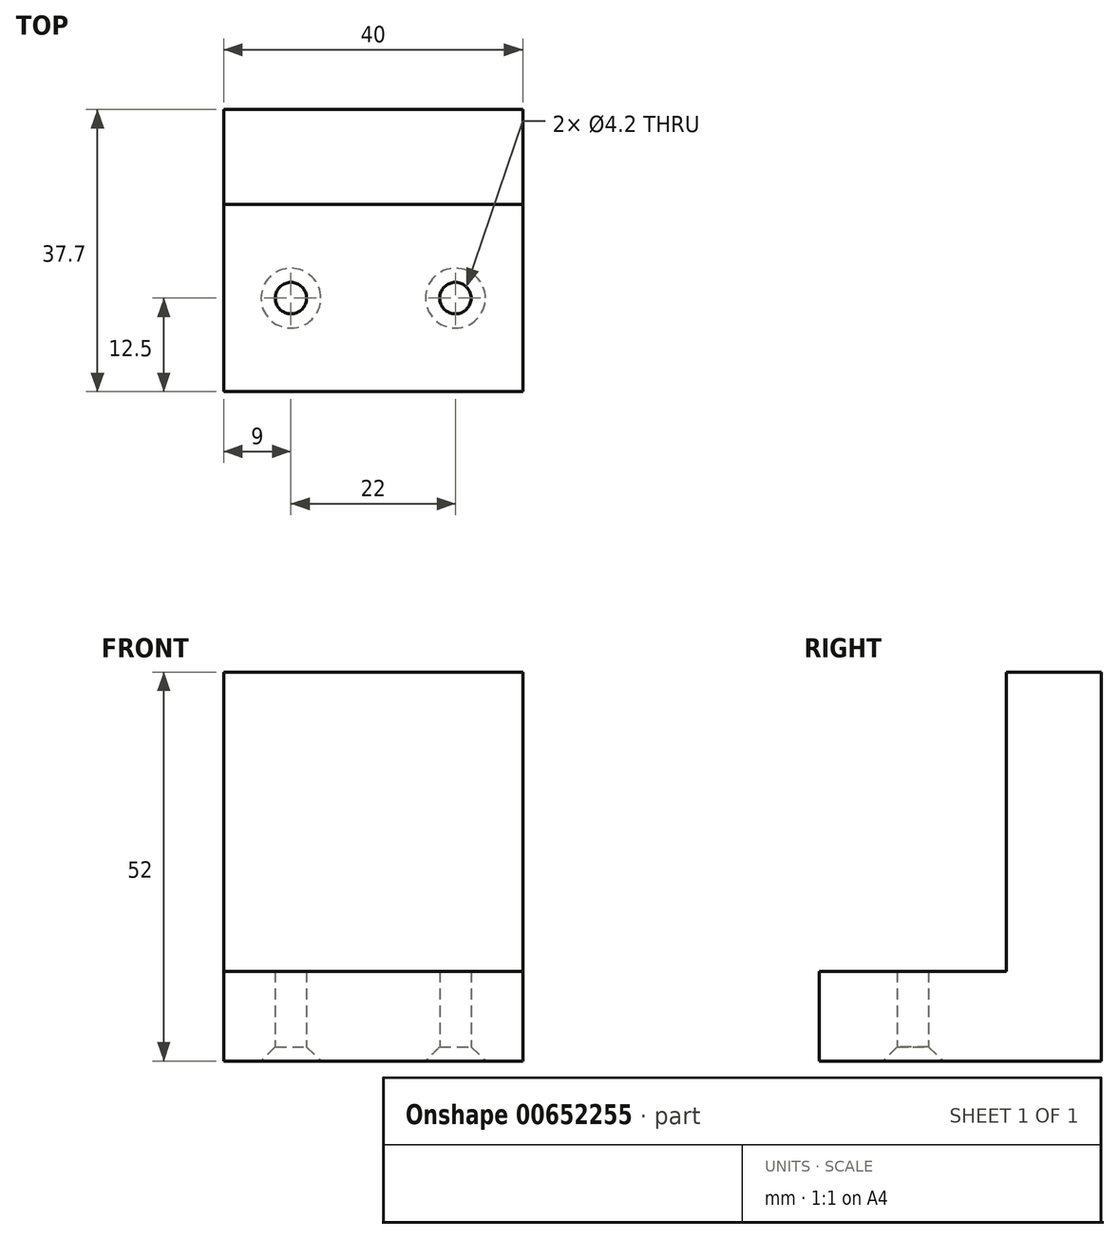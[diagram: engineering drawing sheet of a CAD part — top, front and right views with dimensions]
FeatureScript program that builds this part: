
annotation { "Feature Type Name" : "Feature", "Feature Type Description" : "" }
export const myFeature = defineFeature(function(context is Context, id is Id, definition is map)
    precondition{}
    {
        {
            var Q0;
            Q0=qCreatedBy(makeId("Front.planeOp"),FACE);
            var sketch = newSketch(context, id + "F0", { "sketchPlane" : qUnion([Q0])});
            skLineSegment(sketch, "E0.bottom", {"start": v(0, 0) * mm, "end": v(40, 0) * mm});
            skLineSegment(sketch, "E0.top", {"start": v(0, 52) * mm, "end": v(40, 52) * mm});
            skLineSegment(sketch, "E0.left", {"start": v(0, 0) * mm, "end": v(0, 52) * mm});
            skLineSegment(sketch, "E0.right", {"start": v(40, 0) * mm, "end": v(40, 52) * mm});
            skSolve(sketch);
        }
        {
            var Q0;
            Q0=makeQuery(id+"F0.imprint","IMPRINT",FACE,{"disambiguationData":[TD([[makeQuery(id+"F0.imprint","IMPRINT",EDGE,{"derivedFrom":sQuery(id+"F0.wireOp",EDGE,"E0.bottom")}),1.0]])]});
            extrude(context, id + "F1", {"entities" : qUnion([Q0]), "depth" : 37.7 * mm, "offsetDistance" : 25 * mm});
        }
        {
            var Q0;
            Q0=makeQuery(id+"F1.opExtrude","CAP_FACE",FACE,{"disambiguationData":[OSD([sQuery(id+"F0.wireOp",EDGE,"E0.bottom"),sQuery(id+"F0.wireOp",EDGE,"E0.top"),sQuery(id+"F0.wireOp",EDGE,"E0.left"),sQuery(id+"F0.wireOp",EDGE,"E0.right")])],"isStart":false});
            var sketch = newSketch(context, id + "F2", { "sketchPlane" : qUnion([Q0])});
            skLineSegment(sketch, "E1.bottom", {"start": v(0, 52) * mm, "end": v(40, 52) * mm});
            skLineSegment(sketch, "E1.top", {"start": v(0, 12) * mm, "end": v(40, 12) * mm});
            skLineSegment(sketch, "E1.left", {"start": v(0, 52) * mm, "end": v(0, 12) * mm});
            skLineSegment(sketch, "E1.right", {"start": v(40, 52) * mm, "end": v(40, 12) * mm});
            skSolve(sketch);
        }
        {
            var Q0;
            Q0 = qSketchRegion(id + "F2", true);
            extrude(context, id + "F3", {"entities" : qUnion([Q0]), "operationType" : NewBodyOperationType.REMOVE, "oppositeDirection" : true, "depth" : 25 * mm, "offsetDistance" : 25 * mm});
        }
        {
            var Q0;
            Q0=makeQuery(id+"F1.opExtrude","SWEPT_FACE",FACE,{"disambiguationData":[OSD([sQuery(id+"F0.wireOp",EDGE,"E0.bottom")])]});
            var sketch = newSketch(context, id + "F4", { "sketchPlane" : qUnion([Q0])});
            skLineSegment(sketch, "E2", {"start": v(-14.3, 25.2) * mm, "end": v(55.62, 25.2) * mm, "construction": true});
            skLineSegment(sketch, "E3", {"start": v(20, 43.49) * mm, "end": v(20, -9.67) * mm, "construction": true});
            skPoint(sketch, "E3.startSnap0", {"position": v(20, 37.7) * mm});
            skPoint(sketch, "E3.endSnap0", {"position": v(20, 0) * mm});
            skPoint(sketch, "E4", {"position": v(9, 25.2) * mm});
            skPoint(sketch, "E5", {"position": v(31, 25.2) * mm});
            skSolve(sketch);
        }
        {
            var Q0;
            Q0=sQuery(id+"F4.wireOp",VERTEX,"E4");
            var Q1;
            Q1=sQuery(id+"F4.wireOp",VERTEX,"E5");
            var Q2;
            Q2=makeQuery(id+"F1.opExtrude","SWEPT_BODY",BODY,{"disambiguationData":[OSD([sQuery(id+"F0.wireOp",EDGE,"E0.bottom"),sQuery(id+"F0.wireOp",EDGE,"E0.top"),sQuery(id+"F0.wireOp",EDGE,"E0.left"),sQuery(id+"F0.wireOp",EDGE,"E0.right")])]});
            hole(context, id + "F5", {"style" : HoleStyle.C_SINK, "endStyle" : HoleEndStyle.THROUGH, "holeDiameter" : 4.2 * mm, "cSinkDiameter" : 8 * mm, "cSinkAngle" : 90 * degree, "majorDiameter" : 5 * mm, "isTappedThrough" : true, "tappedDepth" : 12 * mm, "tapClearance" : 3, "locations" : qUnion([Q0, Q1]), "scope" : qUnion([Q2])});
        }
    });
